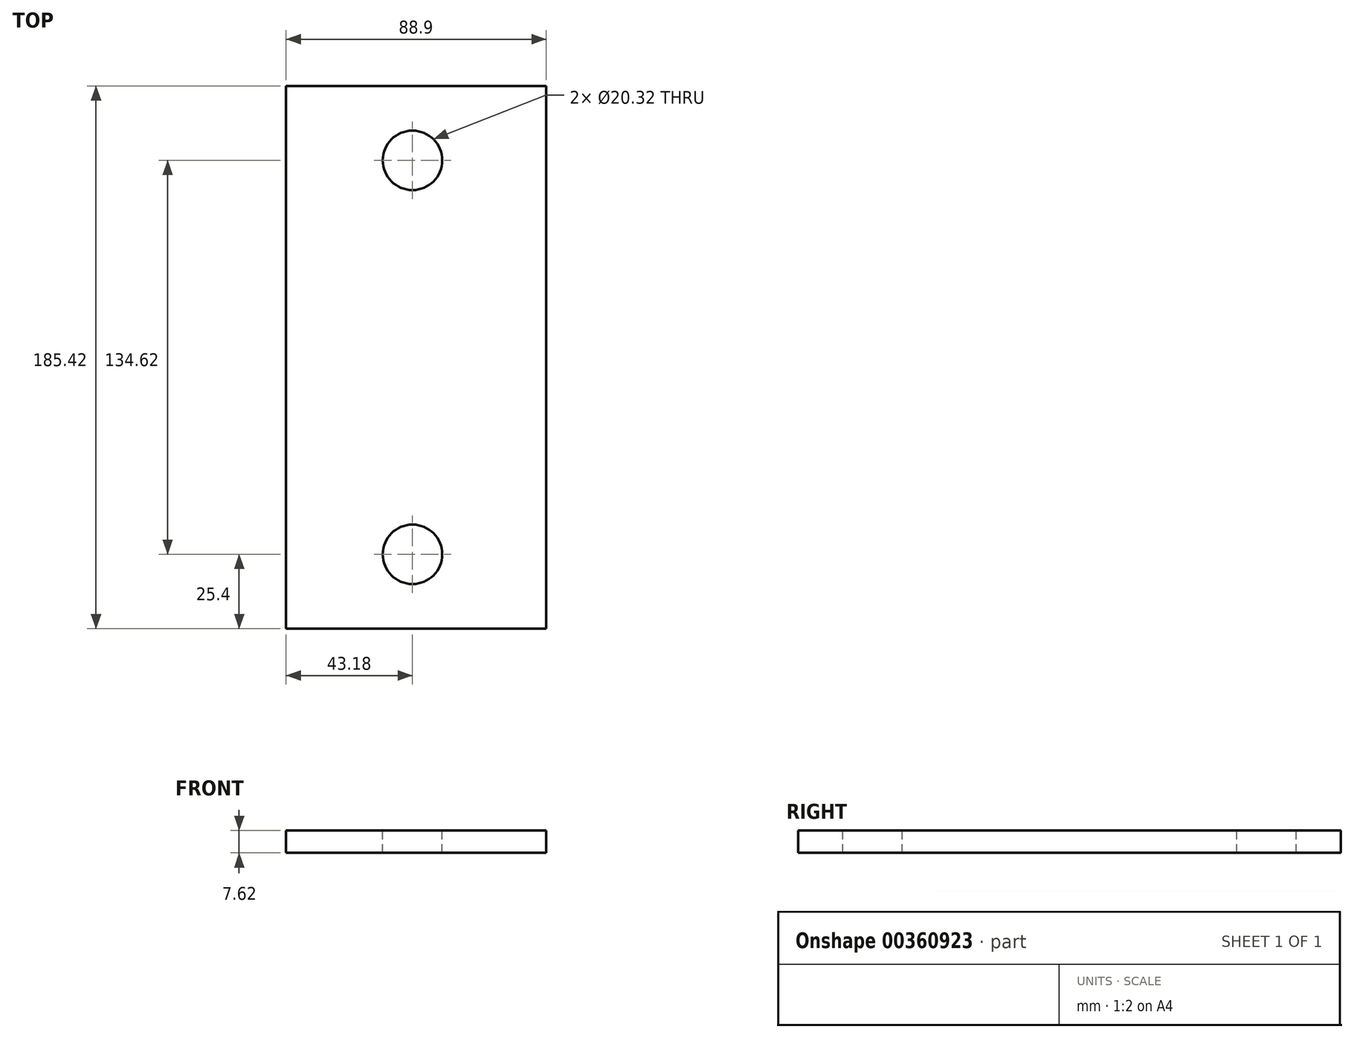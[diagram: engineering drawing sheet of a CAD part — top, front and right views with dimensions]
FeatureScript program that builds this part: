
annotation { "Feature Type Name" : "Feature", "Feature Type Description" : "" }
export const myFeature = defineFeature(function(context is Context, id is Id, definition is map)
    precondition{}
    {
        {
            var Q0;
            Q0=qCreatedBy(makeId("Top.planeOp"),FACE);
            var sketch = newSketch(context, id + "F0", { "sketchPlane" : qUnion([Q0])});
            skLineSegment(sketch, "E0.bottom", {"start": v(0, 0) * mm, "end": v(88.9, 0) * mm});
            skLineSegment(sketch, "E0.top", {"start": v(0, 185.42) * mm, "end": v(88.9, 185.42) * mm});
            skLineSegment(sketch, "E0.left", {"start": v(0, 0) * mm, "end": v(0, 185.42) * mm});
            skLineSegment(sketch, "E0.right", {"start": v(88.9, 0) * mm, "end": v(88.9, 185.42) * mm});
            skSolve(sketch);
        }
        {
            var Q0;
            Q0=makeQuery(id+"F0.imprint","IMPRINT",FACE,{"disambiguationData":[TD([[makeQuery(id+"F0.imprint","IMPRINT",EDGE,{"derivedFrom":sQuery(id+"F0.wireOp",EDGE,"E0.bottom")}),1.0]])]});
            extrude(context, id + "F1", {"entities" : qUnion([Q0]), "depth" : 7.62 * mm});
        }
        {
            var Q0;
            Q0=makeQuery(id+"F1.opExtrude","CAP_FACE",FACE,{"disambiguationData":[OSD([sQuery(id+"F0.wireOp",EDGE,"E0.bottom"),sQuery(id+"F0.wireOp",EDGE,"E0.top"),sQuery(id+"F0.wireOp",EDGE,"E0.left"),sQuery(id+"F0.wireOp",EDGE,"E0.right")])],"isStart":false});
            var sketch = newSketch(context, id + "F2", { "sketchPlane" : qUnion([Q0])});
            skCircle(sketch, "E1", {"center": v(43.18, 160.02) * mm, "radius": 10.16 * mm});
            skCircle(sketch, "E2", {"center": v(43.18, 25.4) * mm, "radius": 10.16 * mm});
            skSolve(sketch);
        }
        {
            var Q0;
            Q0=sQuery(id+"F2.wireOp",VERTEX,"E1.center");
            var Q1;
            Q1=sQuery(id+"F2.wireOp",VERTEX,"E2.center");
            var Q2;
            Q2=makeQuery(id+"F1.opExtrude","SWEPT_BODY",BODY,{"disambiguationData":[OSD([sQuery(id+"F0.wireOp",EDGE,"E0.bottom"),sQuery(id+"F0.wireOp",EDGE,"E0.top"),sQuery(id+"F0.wireOp",EDGE,"E0.left"),sQuery(id+"F0.wireOp",EDGE,"E0.right")])]});
            hole(context, id + "F3", {"style" : HoleStyle.SIMPLE, "endStyle" : HoleEndStyle.THROUGH, "holeDiameter" : 20.32 * mm, "isTappedThrough" : true, "tappedDepth" : 12.7 * mm, "tapClearance" : 3, "locations" : qUnion([Q0, Q1]), "scope" : qUnion([Q2])});
        }
    });
